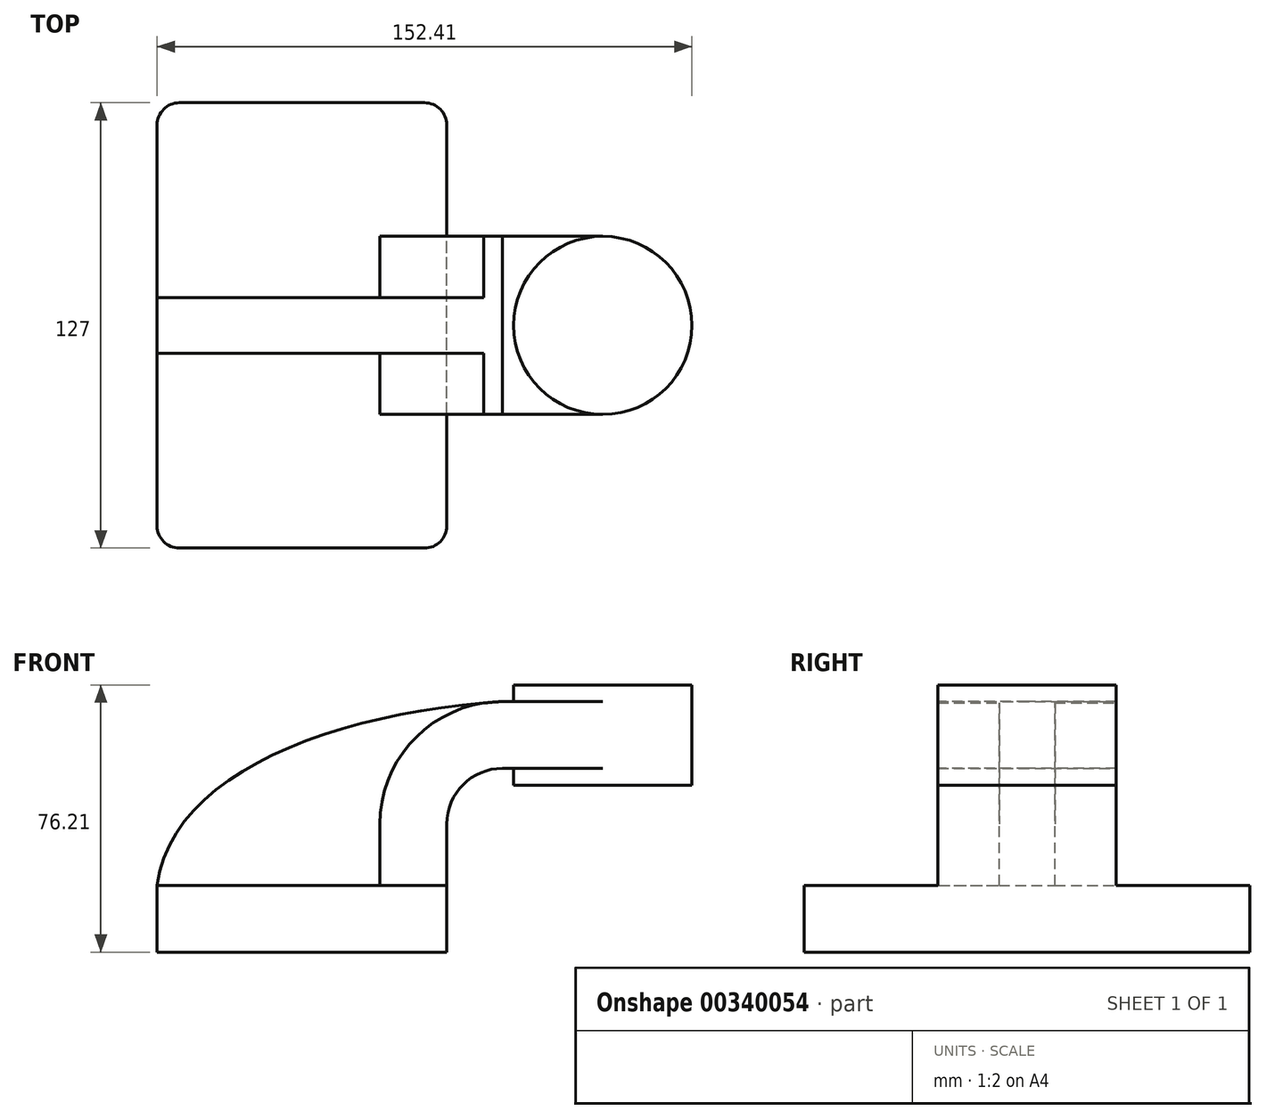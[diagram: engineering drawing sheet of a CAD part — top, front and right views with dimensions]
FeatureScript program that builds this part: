
annotation { "Feature Type Name" : "Feature", "Feature Type Description" : "" }
export const myFeature = defineFeature(function(context is Context, id is Id, definition is map)
    precondition{}
    {
        {
            var Q0;
            Q0=qCreatedBy(makeId("Front.planeOp"),FACE);
            var sketch = newSketch(context, id + "F0", { "sketchPlane" : qUnion([Q0])});
            skLineSegment(sketch, "E0.bottom", {"start": v(41.28, 9.53) * mm, "end": v(-41.28, 9.53) * mm});
            skLineSegment(sketch, "E0.top", {"start": v(41.28, -9.52) * mm, "end": v(-41.28, -9.52) * mm});
            skLineSegment(sketch, "E0.left", {"start": v(41.28, 9.53) * mm, "end": v(41.28, -9.52) * mm});
            skLineSegment(sketch, "E0.right", {"start": v(-41.28, 9.53) * mm, "end": v(-41.28, -9.52) * mm});
            skPoint(sketch, "E0.middle", {"position": v(0, 0) * mm});
            skLineSegment(sketch, "E1.bottom", {"start": v(111.12, 66.68) * mm, "end": v(60.32, 66.68) * mm});
            skLineSegment(sketch, "E1.top", {"start": v(111.12, 38.1) * mm, "end": v(60.32, 38.1) * mm});
            skLineSegment(sketch, "E1.left", {"start": v(111.12, 66.68) * mm, "end": v(111.12, 38.1) * mm});
            skLineSegment(sketch, "E1.right", {"start": v(60.32, 66.68) * mm, "end": v(60.32, 38.1) * mm});
            skPoint(sketch, "E1.middle", {"position": v(85.72, 52.39) * mm});
            skLineSegment(sketch, "E2", {"start": v(41.28, 9.53) * mm, "end": v(41.28, 27) * mm});
            skArc(sketch, "E3", {"start": v(41.27, 27) * mm, "mid": v(45.92, 38.23) * mm, "end": v(57.15, 42.88) * mm});
            skLineSegment(sketch, "E4", {"start": v(57.15, 42.88) * mm, "end": v(85.72, 42.88) * mm});
            skLineSegment(sketch, "E5.0", {"start": v(57.15, 61.93) * mm, "end": v(85.72, 61.93) * mm});
            skArc(sketch, "E5.1", {"start": v(22.22, 27) * mm, "mid": v(32.45, 51.7) * mm, "end": v(57.15, 61.93) * mm});
            skLineSegment(sketch, "E5.2", {"start": v(22.22, 9.53) * mm, "end": v(22.22, 27) * mm});
            skLineSegment(sketch, "E6", {"start": v(85.72, 38.1) * mm, "end": v(85.72, 66.68) * mm});
            skFitSpline(sketch, "E7", {"points": [v(-41.28, 9.53) * mm, v(57.15, 61.93) * mm], "startDerivative": vector(12.8, 96.34) * mm, "endDerivative": vector(145.15, 9.73) * mm});
            skSolve(sketch);
        }
        {
            var Q0;
            Q0=makeQuery(id+"F0.imprint","IMPRINT",FACE,{"disambiguationData":[TD([[makeQuery(id+"F0.imprint","IMPRINT",EDGE,{"derivedFrom":sQuery(id+"F0.wireOp",EDGE,"E0.top")}),-1.0]])]});
            extrude(context, id + "F1", {"entities" : qUnion([Q0]), "endBound" : BoundingType.SYMMETRIC, "depth" : 127 * mm});
        }
        {
            var Q0;
            {var subQ1=sQuery(id+"F0.wireOp",EDGE,"E2");Q0=makeQuery(id+"F0.imprint","IMPRINT",FACE,{"disambiguationData":[TD([[makeQuery(id+"F0.imprint","IMPRINT",EDGE,{"derivedFrom":subQ1}),1.0]])]});}
            var Q1;
            {var subQ0=sQuery(id+"F0.wireOp",EDGE,"E5.0");var subQ1=sQuery(id+"F0.wireOp",EDGE,"E1.right");var subQ2=makeQuery(id+"F0.imprint","INTERSECT",VERTEX,{"derivedFrom":[subQ1,subQ0]});Q1=makeQuery(id+"F0.imprint","IMPRINT",FACE,{"disambiguationData":[TD([[makeQuery(id+"F0.imprint","IMPRINT",EDGE,{"disambiguationData":[TD([[subQ2,-1.0]])],"derivedFrom":subQ1}),1.0]])]});}
            extrude(context, id + "F2", {"entities" : qUnion([Q0, Q1]), "operationType" : NewBodyOperationType.ADD, "endBound" : BoundingType.SYMMETRIC, "depth" : 50.8 * mm});
        }
        {
            var Q0;
            {var subQ3=sQuery(id+"F0.wireOp",EDGE,"E5.2");Q0=makeQuery(id+"F0.imprint","IMPRINT",FACE,{"disambiguationData":[TD([[makeQuery(id+"F0.imprint","IMPRINT",EDGE,{"derivedFrom":subQ3}),1.0]])]});}
            extrude(context, id + "F3", {"entities" : qUnion([Q0]), "operationType" : NewBodyOperationType.ADD, "endBound" : BoundingType.SYMMETRIC, "depth" : 15.88 * mm});
        }
        {
            var Q0;
            {var subQ0=sQuery(id+"F0.wireOp",EDGE,"E1.left");Q0=makeQuery(id+"F0.imprint","IMPRINT",FACE,{"disambiguationData":[TD([[makeQuery(id+"F0.imprint","IMPRINT",EDGE,{"derivedFrom":subQ0}),-1.0]])]});}
            var Q1;
            Q1=sQuery(id+"F0.wireOp",EDGE,"E6");
            revolve(context, id + "F4", {"operationType" : NewBodyOperationType.ADD, "entities" : qUnion([Q0]), "axis" : qUnion([Q1]), "revolveType" : RevolveType.FULL});
        }
        {
            var Q0;
            Q0=makeQuery(id+"F1.opExtrude","CAP_EDGE",EDGE,{"disambiguationData":[OSD([sQuery(id+"F0.wireOp",EDGE,"E0.left")])],"isStart":false});
            var Q1;
            Q1=makeQuery(id+"F1.opExtrude","CAP_EDGE",EDGE,{"disambiguationData":[OSD([sQuery(id+"F0.wireOp",EDGE,"E0.left")])],"isStart":true});
            var Q2;
            Q2=makeQuery(id+"F1.opExtrude","CAP_EDGE",EDGE,{"disambiguationData":[OSD([sQuery(id+"F0.wireOp",EDGE,"E0.right")])],"isStart":true});
            var Q3;
            Q3=makeQuery(id+"F1.opExtrude","CAP_EDGE",EDGE,{"disambiguationData":[OSD([sQuery(id+"F0.wireOp",EDGE,"E0.right")])],"isStart":false});
            fillet(context, id + "F5", {"entities" : qUnion([Q0, Q1, Q2, Q3]), "radius" : 6.35 * mm, "tangentPropagation" : true, "allowEdgeOverflow" : false});
        }
    });
